AUTODESK INVENTOR PART (.ipt)
format: ipt  version: 2019.4 (Build 234330000, 330)  size: 292,352 bytes
history: native  units: mm
features: sketch x8, extrude x7, chamfer x3, other x1, hole x1, fillet x1
ambient origin geometry x8: Origin, YZ Plane, XZ Plane, XY Plane, X Axis, Y Axis, Z Axis, Center Point
bodies: Body1 (feature_tree)
feature tree (21):
  other  "ソリッド1"
  extrude  "押し出し1"  Depth=2.0mm
  hole  "穴1"  [1 undecoded]
  extrude  "押し出し2"  Depth=2.0mm
  extrude  "押し出し3"  Depth=2.0mm
  extrude  "押し出し4"  Depth=2.0mm
  extrude  "押し出し5"  Depth=2.0mm
  extrude  "押し出し6"  Depth=2.0mm
  fillet  "フィレット1"  Radius=2.0mm
  chamfer  "面取り1"  Distance=28.5mm
  chamfer  "面取り2"  Distance=46.5mm
  extrude  "押し出し7"  Depth=11.25mm
  chamfer  "面取り3"  Distance=8.0mm
  sketch  "スケッチ1"
  sketch  "スケッチ2"
  sketch  "スケッチ3"
  sketch  "スケッチ4"
  sketch  "スケッチ5"
  sketch  "スケッチ6"
  sketch  "スケッチ7"
  sketch  "スケッチ8"
note: 1 required parameter value undecoded (feature->parameter linkage not recoverable at this tier; creation-order binding heuristic only, values carry confidence <= 0.55)
